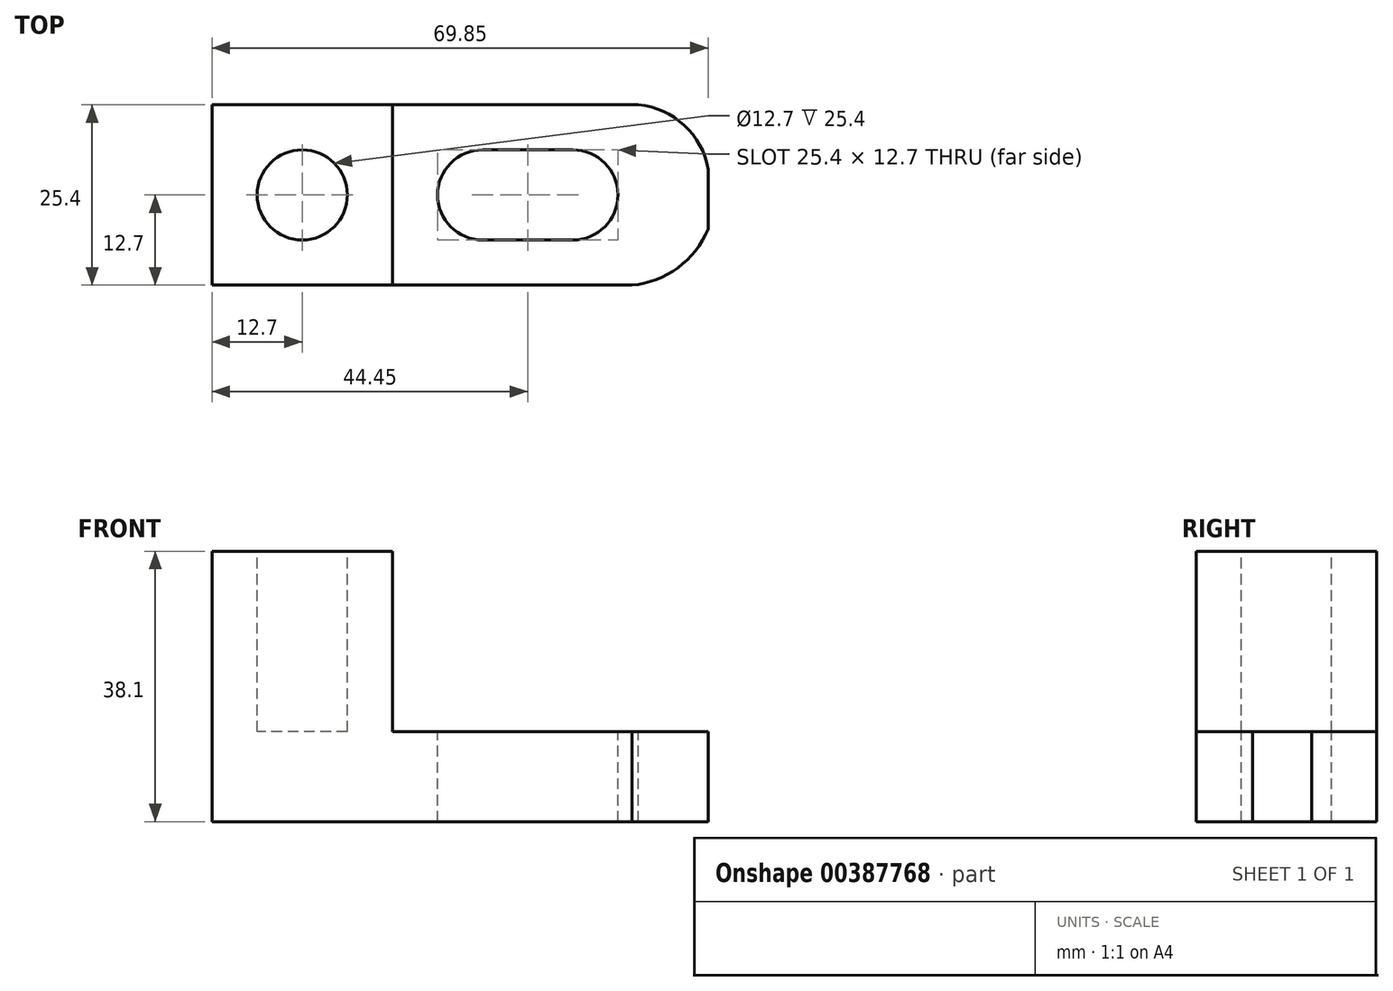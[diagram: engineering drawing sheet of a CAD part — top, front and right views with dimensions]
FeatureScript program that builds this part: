
annotation { "Feature Type Name" : "Feature", "Feature Type Description" : "" }
export const myFeature = defineFeature(function(context is Context, id is Id, definition is map)
    precondition{}
    {
        {
            var Q0;
            Q0=qCreatedBy(makeId("Front.planeOp"),FACE);
            var sketch = newSketch(context, id + "F0", { "sketchPlane" : qUnion([Q0])});
            skLineSegment(sketch, "E0", {"start": v(0, 0) * mm, "end": v(69.85, 0) * mm});
            skLineSegment(sketch, "E1", {"start": v(69.85, 0) * mm, "end": v(69.85, 12.7) * mm});
            skLineSegment(sketch, "E2", {"start": v(69.85, 12.7) * mm, "end": v(25.4, 12.7) * mm});
            skLineSegment(sketch, "E3", {"start": v(25.4, 12.7) * mm, "end": v(25.4, 38.1) * mm});
            skLineSegment(sketch, "E4", {"start": v(25.4, 38.1) * mm, "end": v(0, 38.1) * mm});
            skLineSegment(sketch, "E5", {"start": v(0, 38.1) * mm, "end": v(0, 0) * mm});
            skSolve(sketch);
        }
        {
            var Q0;
            Q0=makeQuery(id+"F0.imprint","IMPRINT",FACE,{"disambiguationData":[TD([[makeQuery(id+"F0.imprint","IMPRINT",EDGE,{"derivedFrom":sQuery(id+"F0.wireOp",EDGE,"E0")}),1.0]])]});
            extrude(context, id + "F1", {"entities" : qUnion([Q0]), "depth" : 25.4 * mm});
        }
        {
            var Q0;
            Q0=makeQuery(id+"F1.opExtrude","SWEPT_FACE",FACE,{"disambiguationData":[OSD([sQuery(id+"F0.wireOp",EDGE,"E2")])]});
            var sketch = newSketch(context, id + "F2", { "sketchPlane" : qUnion([Q0])});
            skArc(sketch, "E6", {"start": v(69.85, -12.7) * mm, "mid": v(67.71, -4.21) * mm, "end": v(60.04, 0) * mm});
            skArc(sketch, "E7", {"start": v(59.1, -25.4) * mm, "mid": v(65.6, -22.96) * mm, "end": v(69.85, -17.48) * mm});
            skSolve(sketch);
        }
        {
            var Q0;
            {var subQ0=sQuery(id+"F2.wireOp",EDGE,"E6");var subQ1=sQuery(id+"F0.wireOp",EDGE,"E2");var subQ2=makeQuery(id+"F1.opExtrude","CAP_EDGE",EDGE,{"disambiguationData":[OSD([subQ1])],"isStart":true});var subQ3=makeQuery(id+"F2.imprint","INTERSECT",VERTEX,{"derivedFrom":[subQ2,subQ0]});Q0=makeQuery(id+"F2.imprint","IMPRINT",FACE,{"disambiguationData":[TD([[makeQuery(id+"F2.imprint","IMPRINT",EDGE,{"disambiguationData":[TD([[subQ3,1.0]])],"derivedFrom":subQ0}),-1.0]])]});}
            var Q1;
            {var subQ0=sQuery(id+"F2.wireOp",EDGE,"E7");Q1=makeQuery(id+"F2.imprint","IMPRINT",FACE,{"disambiguationData":[TD([[makeQuery(id+"F2.imprint","IMPRINT",EDGE,{"derivedFrom":subQ0}),-1.0]])]});}
            extrude(context, id + "F3", {"entities" : qUnion([Q0, Q1]), "operationType" : NewBodyOperationType.REMOVE, "oppositeDirection" : true, "depth" : 25.4 * mm});
        }
        {
            var Q0;
            Q0=makeQuery(id+"F1.opExtrude","SWEPT_FACE",FACE,{"disambiguationData":[OSD([sQuery(id+"F0.wireOp",EDGE,"E4")])]});
            var sketch = newSketch(context, id + "F4", { "sketchPlane" : qUnion([Q0])});
            skCircle(sketch, "E8", {"center": v(12.7, -12.7) * mm, "radius": 6.35 * mm});
            skPoint(sketch, "E8.centerSnap0", {"position": v(12.7, 0) * mm});
            skPoint(sketch, "E8.centerSnap1", {"position": v(0, -12.7) * mm});
            skSolve(sketch);
        }
        {
            var Q0;
            Q0=makeQuery(id+"F4.imprint","IMPRINT",FACE,{"disambiguationData":[TD([[makeQuery(id+"F4.imprint","IMPRINT",EDGE,{"derivedFrom":sQuery(id+"F4.wireOp",EDGE,"E8")}),1.0]])]});
            extrude(context, id + "F5", {"entities" : qUnion([Q0]), "operationType" : NewBodyOperationType.REMOVE, "oppositeDirection" : true, "depth" : 25.4 * mm});
        }
        {
            var Q0;
            Q0=makeQuery(id+"F1.opExtrude","SWEPT_FACE",FACE,{"disambiguationData":[OSD([sQuery(id+"F0.wireOp",EDGE,"E2")])]});
            var sketch = newSketch(context, id + "F6", { "sketchPlane" : qUnion([Q0])});
            skCircle(sketch, "E9", {"center": v(38.1, -12.7) * mm, "radius": 6.35 * mm});
            skCircle(sketch, "E10", {"center": v(50.8, -12.7) * mm, "radius": 6.35 * mm});
            skLineSegment(sketch, "E11", {"start": v(38.1, -6.35) * mm, "end": v(50.8, -6.35) * mm});
            skLineSegment(sketch, "E12", {"start": v(38.1, -19.05) * mm, "end": v(50.8, -19.05) * mm});
            skSolve(sketch);
        }
        {
            var Q0;
            {var subQ0=sQuery(id+"F6.wireOp",EDGE,"E9");var subQ1=makeQuery(id+"F6.imprint","INTERSECT",VERTEX,{"derivedFrom":[subQ0,sQuery(id+"F6.wireOp",EDGE,"E11")]});Q0=makeQuery(id+"F6.imprint","IMPRINT",FACE,{"disambiguationData":[TD([[makeQuery(id+"F6.imprint","IMPRINT",EDGE,{"disambiguationData":[TD([[subQ1,1.0]])],"derivedFrom":subQ0}),1.0]])]});}
            var Q1;
            {var subQ0=sQuery(id+"F6.wireOp",EDGE,"E10");var subQ1=makeQuery(id+"F6.imprint","INTERSECT",VERTEX,{"derivedFrom":[subQ0,sQuery(id+"F6.wireOp",EDGE,"E11")]});Q1=makeQuery(id+"F6.imprint","IMPRINT",FACE,{"disambiguationData":[TD([[makeQuery(id+"F6.imprint","IMPRINT",EDGE,{"disambiguationData":[TD([[subQ1,-1.0]])],"derivedFrom":subQ0}),1.0]])]});}
            var Q2;
            {var subQ0=sQuery(id+"F6.wireOp",EDGE,"E12");Q2=makeQuery(id+"F6.imprint","IMPRINT",FACE,{"disambiguationData":[TD([[makeQuery(id+"F6.imprint","IMPRINT",EDGE,{"derivedFrom":subQ0}),1.0]])]});}
            var Q3;
            {var subQ0=sQuery(id+"F6.wireOp",EDGE,"E11");Q3=makeQuery(id+"F6.imprint","IMPRINT",FACE,{"disambiguationData":[TD([[makeQuery(id+"F6.imprint","IMPRINT",EDGE,{"derivedFrom":subQ0}),-1.0]])]});}
            extrude(context, id + "F7", {"entities" : qUnion([Q0, Q1, Q2, Q3]), "operationType" : NewBodyOperationType.REMOVE, "oppositeDirection" : true, "depth" : 25.4 * mm});
        }
    });
